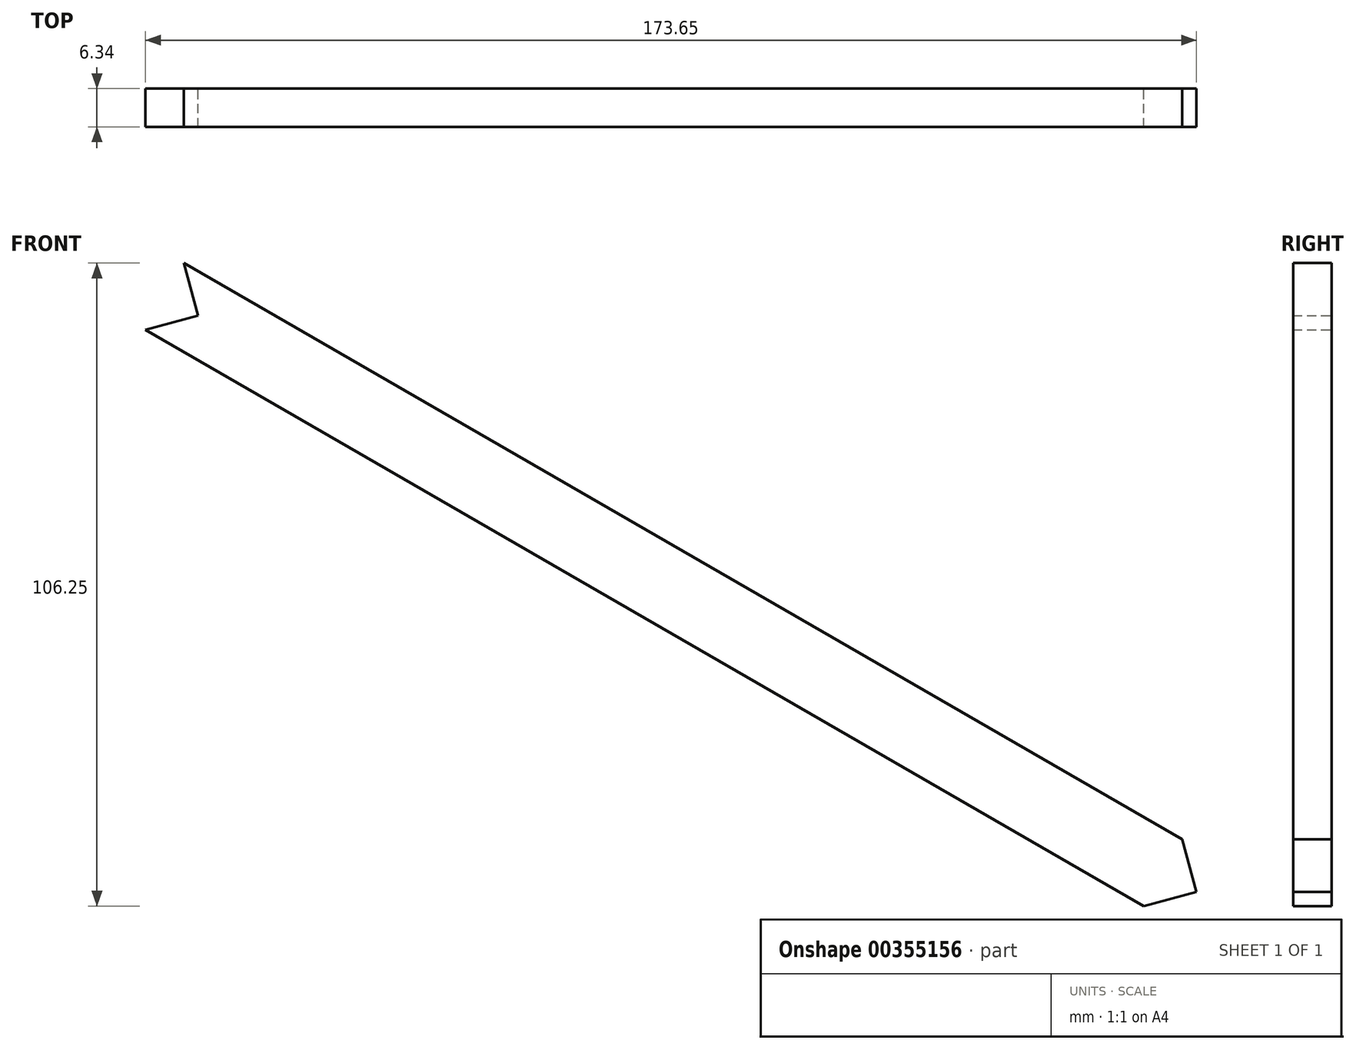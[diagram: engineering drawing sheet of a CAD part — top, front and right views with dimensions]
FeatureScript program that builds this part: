
annotation { "Feature Type Name" : "Feature", "Feature Type Description" : "" }
export const myFeature = defineFeature(function(context is Context, id is Id, definition is map)
    precondition{}
    {
        {
            var Q0;
            Q0=qCreatedBy(makeId("Front.planeOp"),FACE);
            var sketch = newSketch(context, id + "F0", { "sketchPlane" : qUnion([Q0])});
            skLineSegment(sketch, "E0", {"start": v(-87.99, -152.4) * mm, "end": v(263.96, -152.4) * mm, "construction": true});
            skLineSegment(sketch, "E1", {"start": v(263.96, -152.4) * mm, "end": v(0, 0) * mm});
            skLineSegment(sketch, "E2", {"start": v(0, 0) * mm, "end": v(-87.99, -152.4) * mm, "construction": true});
            skLineSegment(sketch, "E3", {"start": v(0, 0) * mm, "end": v(-152.4, 87.99) * mm});
            skCircle(sketch, "E4", {"center": v(0, 0) * mm, "radius": 12.7 * mm});
            skCircle(sketch, "E5", {"center": v(0, 0) * mm, "radius": 9.53 * mm});
            skLineSegment(sketch, "E6", {"start": v(0, 0) * mm, "end": v(6.35, 11) * mm, "construction": true});
            skLineSegment(sketch, "E7", {"start": v(-152.4, 87.99) * mm, "end": v(-146.05, 98.99) * mm});
            skLineSegment(sketch, "E8", {"start": v(-146.05, 98.99) * mm, "end": v(6.35, 11) * mm});
            skLineSegment(sketch, "E9", {"start": v(6.35, 11) * mm, "end": v(270.31, -141.4) * mm});
            skLineSegment(sketch, "E10", {"start": v(270.31, -141.4) * mm, "end": v(263.96, -152.4) * mm});
            skLineSegment(sketch, "E11", {"start": v(-149.23, 93.49) * mm, "end": v(267.14, -146.9) * mm});
            skLineSegment(sketch, "E12", {"start": v(18.93, 3.74) * mm, "end": v(21.25, -4.94) * mm});
            skLineSegment(sketch, "E13", {"start": v(21.25, -4.94) * mm, "end": v(12.58, -7.26) * mm});
            skLineSegment(sketch, "E14", {"start": v(12.58, -7.26) * mm, "end": v(18.93, 3.74) * mm});
            skLineSegment(sketch, "E15", {"start": v(183.9, -91.51) * mm, "end": v(186.23, -100.19) * mm});
            skLineSegment(sketch, "E16", {"start": v(186.23, -100.19) * mm, "end": v(177.56, -102.51) * mm});
            skLineSegment(sketch, "E17", {"start": v(183.9, -91.51) * mm, "end": v(177.56, -102.51) * mm});
            skSolve(sketch);
        }
        {
            var Q0;
            {var subQ0=sQuery(id+"F0.wireOp",EDGE,"E12");Q0=makeQuery(id+"F0.imprint","IMPRINT",FACE,{"disambiguationData":[TD([[makeQuery(id+"F0.imprint","IMPRINT",EDGE,{"derivedFrom":subQ0}),1.0]])]});}
            var Q1;
            {var subQ0=sQuery(id+"F0.wireOp",EDGE,"E13");Q1=makeQuery(id+"F0.imprint","IMPRINT",FACE,{"disambiguationData":[TD([[makeQuery(id+"F0.imprint","IMPRINT",EDGE,{"derivedFrom":subQ0}),1.0]])]});}
            var Q2;
            {var subQ0=sQuery(id+"F0.wireOp",EDGE,"E15");Q2=makeQuery(id+"F0.imprint","IMPRINT",FACE,{"disambiguationData":[TD([[makeQuery(id+"F0.imprint","IMPRINT",EDGE,{"derivedFrom":subQ0}),-1.0]])]});}
            var Q3;
            {var subQ0=sQuery(id+"F0.wireOp",EDGE,"E16");Q3=makeQuery(id+"F0.imprint","IMPRINT",FACE,{"disambiguationData":[TD([[makeQuery(id+"F0.imprint","IMPRINT",EDGE,{"derivedFrom":subQ0}),-1.0]])]});}
            extrude(context, id + "F1", {"entities" : qUnion([Q0, Q1, Q2, Q3]), "endBound" : BoundingType.SYMMETRIC, "depth" : 6.35 * mm});
        }
    });
